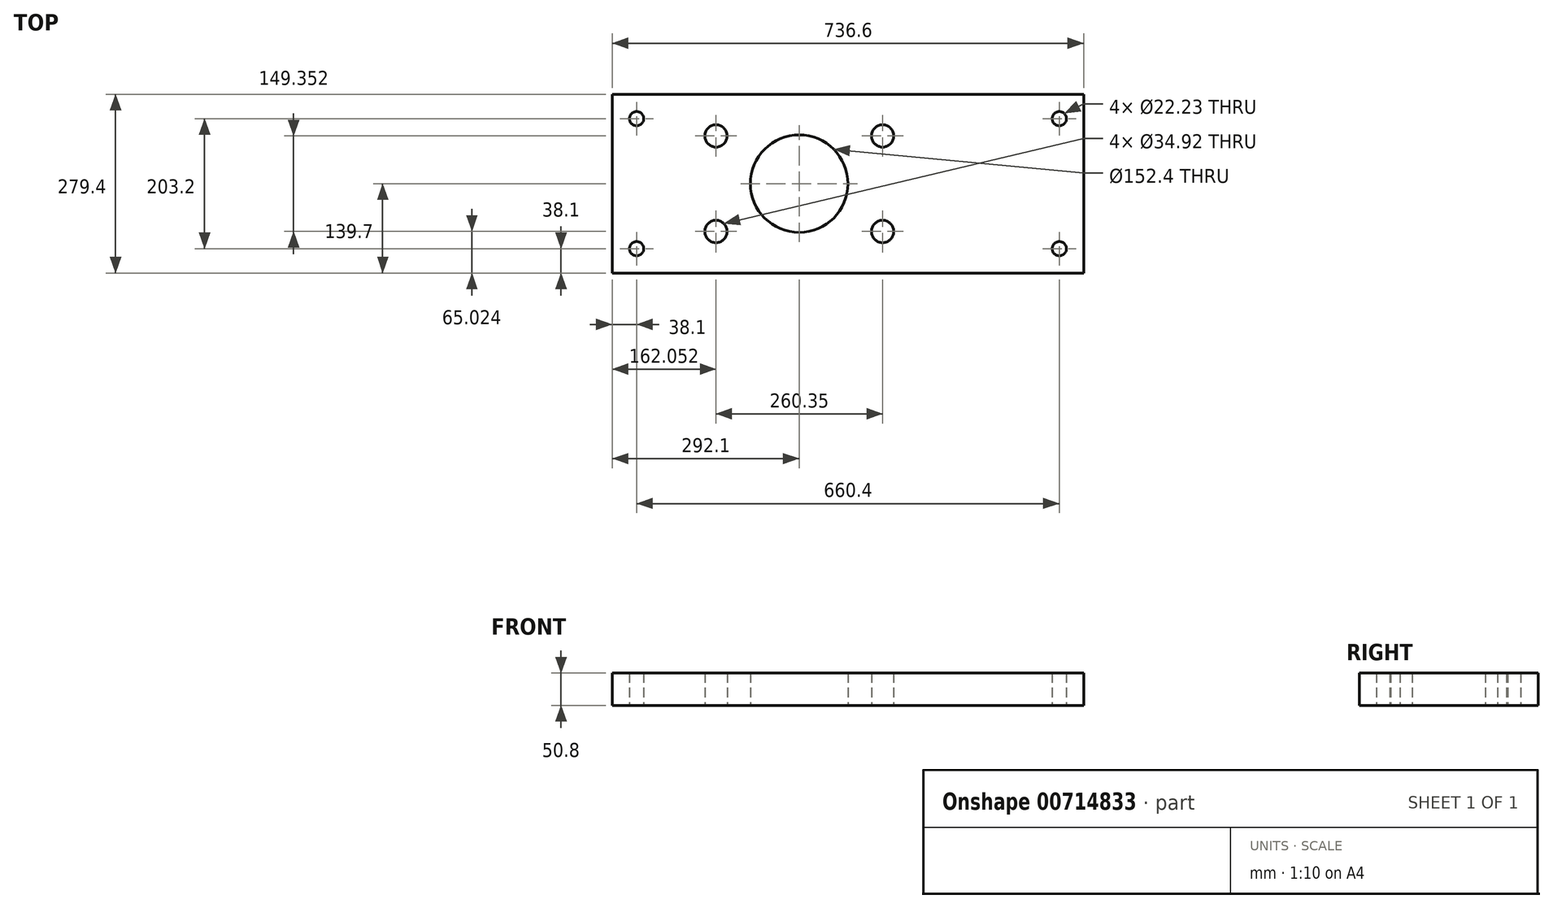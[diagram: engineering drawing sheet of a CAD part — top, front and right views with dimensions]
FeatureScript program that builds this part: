
annotation { "Feature Type Name" : "Feature", "Feature Type Description" : "" }
export const myFeature = defineFeature(function(context is Context, id is Id, definition is map)
    precondition{}
    {
        {
            var Q0;
            Q0=qCreatedBy(makeId("Top.planeOp"),FACE);
            var sketch = newSketch(context, id + "F0", { "sketchPlane" : qUnion([Q0])});
            skLineSegment(sketch, "E0.bottom", {"start": v(-368.3, 139.7) * mm, "end": v(368.3, 139.7) * mm});
            skLineSegment(sketch, "E0.top", {"start": v(-368.3, -139.7) * mm, "end": v(368.3, -139.7) * mm});
            skLineSegment(sketch, "E0.left", {"start": v(-368.3, 139.7) * mm, "end": v(-368.3, -139.7) * mm});
            skLineSegment(sketch, "E0.right", {"start": v(368.3, 139.7) * mm, "end": v(368.3, -139.7) * mm});
            skPoint(sketch, "E0.middle", {"position": v(0, 0) * mm});
            skLineSegment(sketch, "E1.0", {"start": v(-330.2, 139.7) * mm, "end": v(-330.2, -139.7) * mm, "construction": true});
            skLineSegment(sketch, "E2.0", {"start": v(330.2, 139.7) * mm, "end": v(330.2, -139.7) * mm, "construction": true});
            skLineSegment(sketch, "E3", {"start": v(-515.89, 0) * mm, "end": v(476.73, 0) * mm, "construction": true});
            skLineSegment(sketch, "E4.0", {"start": v(-515.89, -101.6) * mm, "end": v(476.73, -101.6) * mm, "construction": true});
            skCircle(sketch, "E5", {"center": v(-330.2, -101.6) * mm, "radius": 11.11 * mm});
            skCircle(sketch, "E6.0.1.0", {"center": v(-330.2, 101.6) * mm, "radius": 11.11 * mm});
            skCircle(sketch, "E6.1.0.0", {"center": v(330.2, -101.6) * mm, "radius": 11.11 * mm});
            skCircle(sketch, "E6.1.1.0", {"center": v(330.2, 101.6) * mm, "radius": 11.11 * mm});
            skLineSegment(sketch, "E6.direction1", {"start": v(-330.2, -101.6) * mm, "end": v(330.2, -101.6) * mm, "construction": true});
            skLineSegment(sketch, "E6.direction2", {"start": v(-330.2, -101.6) * mm, "end": v(-330.2, 101.6) * mm, "construction": true});
            skLineSegment(sketch, "E7.0", {"start": v(-76.2, -101.6) * mm, "end": v(-76.2, 101.6) * mm, "construction": true});
            skCircle(sketch, "E8", {"center": v(-76.2, 0) * mm, "radius": 76.2 * mm});
            skLineSegment(sketch, "E9.0", {"start": v(-206.25, -101.6) * mm, "end": v(-206.25, 101.6) * mm, "construction": true});
            skLineSegment(sketch, "E10.0", {"start": v(-515.89, 74.68) * mm, "end": v(476.73, 74.68) * mm, "construction": true});
            skCircle(sketch, "E11", {"center": v(-206.25, 74.68) * mm, "radius": 17.46 * mm});
            skCircle(sketch, "E12.0.1.0", {"center": v(-206.25, -74.68) * mm, "radius": 17.46 * mm});
            skCircle(sketch, "E12.1.0.0", {"center": v(54.1, 74.68) * mm, "radius": 17.46 * mm});
            skCircle(sketch, "E12.1.1.0", {"center": v(54.1, -74.68) * mm, "radius": 17.46 * mm});
            skLineSegment(sketch, "E12.direction1", {"start": v(-206.25, 74.68) * mm, "end": v(54.1, 74.68) * mm, "construction": true});
            skLineSegment(sketch, "E12.direction2", {"start": v(-206.25, 74.68) * mm, "end": v(-206.25, -74.68) * mm, "construction": true});
            skSolve(sketch);
        }
        {
            var Q0;
            Q0=makeQuery(id+"F0.imprint","IMPRINT",FACE,{"disambiguationData":[TD([[makeQuery(id+"F0.imprint","IMPRINT",EDGE,{"derivedFrom":sQuery(id+"F0.wireOp",EDGE,"E0.bottom")}),-1.0]])]});
            extrude(context, id + "F1", {"entities" : qUnion([Q0]), "depth" : 50.8 * mm, "offsetDistance" : 25.4 * mm});
        }
    });
